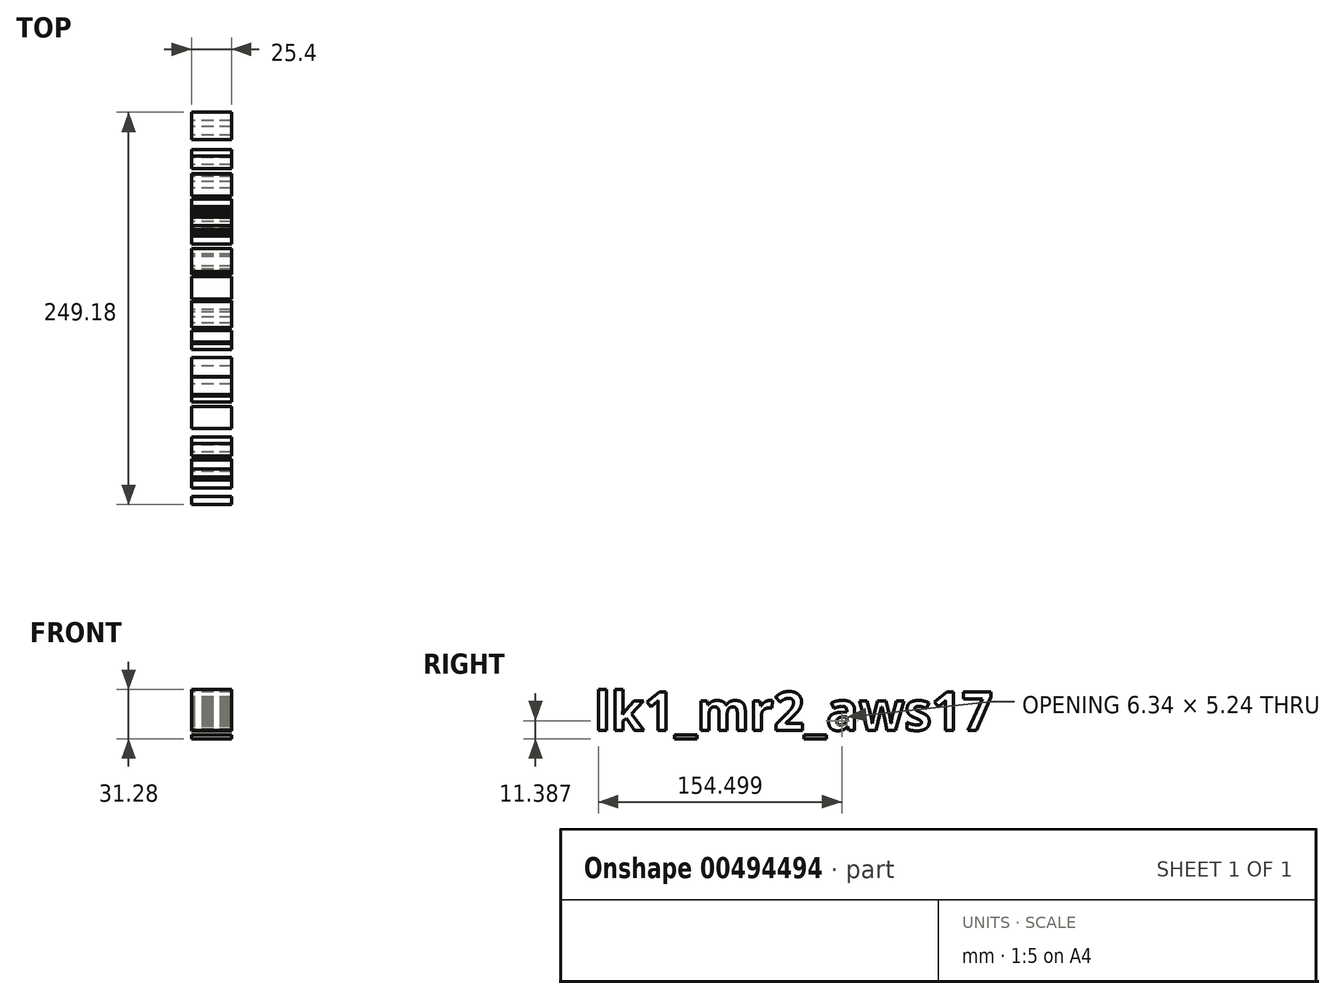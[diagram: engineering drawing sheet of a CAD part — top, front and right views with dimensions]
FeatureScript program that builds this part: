
annotation { "Feature Type Name" : "Feature", "Feature Type Description" : "" }
export const myFeature = defineFeature(function(context is Context, id is Id, definition is map)
    precondition{}
    {
        {
            var Q0;
            Q0=qCreatedBy(makeId("Right.planeOp"),FACE);
            var sketch = newSketch(context, id + "F0", { "sketchPlane" : qUnion([Q0])});
            skText(sketch, "E0", { "text": "lk1_mr2_aws17", "fontName": "OpenSans-Bold.ttf"});
            const initialGuessF0  = {"E0": [-0.127, 0, 1, 0, 0.02453]};
            skSetInitialGuess(sketch, initialGuessF0);
            skSolve(sketch);
        }
        {
            var Q0;
            Q0 = qSketchRegion(id + "F0", true);
            extrude(context, id + "F1", {"entities" : qUnion([Q0]), "depth" : 25.4 * mm});
        }
    });
